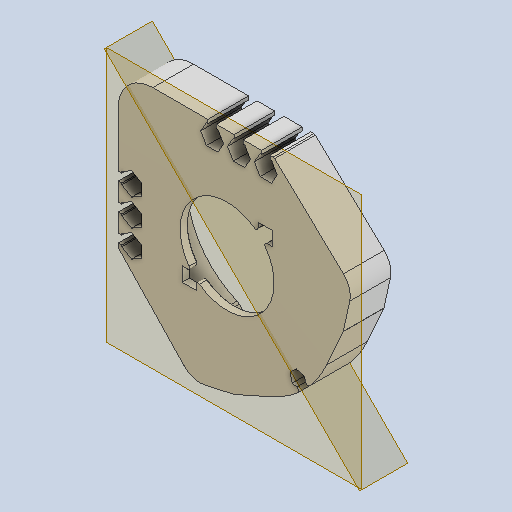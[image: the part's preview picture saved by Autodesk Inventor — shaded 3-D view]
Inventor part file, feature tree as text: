
AUTODESK INVENTOR PART (.ipt)
format: ipt  version: 2022 (Build 260153000, 153)  size: 321,536 bytes
history: native  units: in
note: dims shown in document units (in); Inventor stores cm internally (conversion verified against a paired STEP export)
features: other x3, sketch x3, plane x2
ambient origin geometry x8: Origin, YZ Plane, XZ Plane, XY Plane, X Axis, Y Axis, Z Axis, Center Point
bodies: Solid1 (feature_tree)
feature tree (8):
  other  "uppermidblock.ipt"
  other  "Solid1::uppermidblock.ipt"
  other  "TaggingFeature1"
  sketch  "Sketch1"  dims[d0=0.3937in]
  sketch  "Sketch2"
  sketch  "Sketch3"
  plane  "Work Plane1"
  plane  "Work Plane2"
